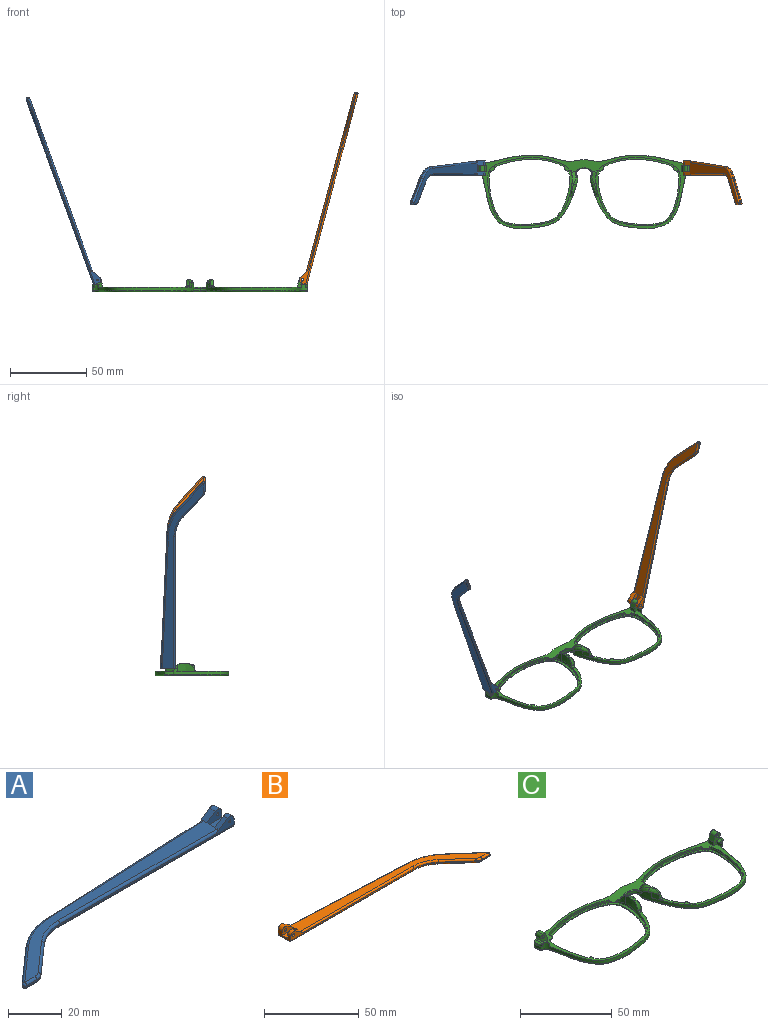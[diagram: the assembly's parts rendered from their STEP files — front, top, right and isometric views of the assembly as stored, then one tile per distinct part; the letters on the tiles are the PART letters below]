
ASSEMBLY  parts=3 mates=2
PART A: 43 faces, bbox 130.2x29.5x5.9 mm
  f0: plane 9.62x3.72mm, normal (1,0,0), area 24.7mm2, adj f1,f3,f4,f5,f10,f16,f18,f28
  f1: cylinder r=2.2mm len=3.45mm, axis (0,-1,0), area 11mm2, adj f0,f2,f4,f37
  f2: plane 6.01x3.91mm, normal (-0.55,0,0.84), area 12.7mm2, adj f1,f4,f9,f19,f37
  f3: plane 2.26x0.1mm, normal (0,0,1), area 0.1mm2, adj f0,f5,f18
  f4: plane 92.1x4.9mm, normal (0,-1,0), area 79.9mm2, adj f0,f1,f2,f14,f19,f36,f42
  f5: plane 93.42x4.13mm, normal (-0.04,1,0), area 64.8mm2, adj f0,f3,f11,f15,f17,f27,f28
  f6: plane 17.82x15.72mm, normal (-0.66,0.75,0), area 14.3mm2, adj f11,f12,f25,f30
  f7: plane 5.46x0.6mm, normal (0,-1,0), area 3.3mm2, adj f12,f13,f23,f32
  f8: plane 14.99x13.23mm, normal (0.66,-0.75,0), area 12mm2, adj f13,f14,f21,f34
  f9: plane 121.18x26.73mm, normal (0,0,1), area 627.7mm2, adj f2,f17,f19,f20,f21,f22,f23,f25
  f10: plane 129.1x27.08mm, normal (0,0,-1), area 686.5mm2, adj f0,f28,f29,f30,f32,f33,f34,f35
  f11: cylinder r=30mm len=18.52mm, axis (0,0,-1), area 12.2mm2, adj f5,f6,f26,f29
  f12: cylinder r=1mm len=1.75mm, axis (0,0,-1), area 1.5mm2, adj f6,f7,f24,f31
  f13: cylinder r=5mm len=3.31mm, axis (0,0,-1), area 2.2mm2, adj f7,f8,f22,f33
  f14: cylinder r=20mm len=13.23mm, axis (0,0,1), area 8.7mm2, adj f4,f8,f20,f35
  f15: plane 5.66x0.25mm, normal (0,0,-1), area 0.7mm2, adj f5,f17,f18
  f16: cylinder r=2.2mm len=3.45mm, axis (0,-1,0), area 14.8mm2, adj f0,f17,f18,f38
  f17: plane 6.01x3.91mm, normal (-0.55,0,0.84), area 16.9mm2, adj f5,f9,f15,f16,f18,f27,f38
  f18: plane 7.92x3.3mm, normal (0,1,0), area 15.9mm2, adj f0,f3,f15,f16,f17,f41
  f19: cylinder r=1mm len=84.18mm, axis (-1,0,0), area 131.4mm2, adj f2,f4,f9,f20
  f20: torus R=21mm, axis (0,0,1), area 23.1mm2, adj f9,f14,f19,f21
  f21: cylinder r=1mm len=15.65mm, axis (-0.75,-0.66,0), area 31.4mm2, adj f8,f9,f20,f22
  f22: torus R=4mm, axis (0,0,1), area 5.3mm2, adj f9,f13,f21,f23
  f23: cylinder r=1mm len=5.46mm, axis (-1,0,0), area 8.6mm2, adj f7,f9,f22,f24
  f24: sphere r=1mm, area 2.4mm2, adj f12,f23,f25
  f25: cylinder r=1mm len=18.48mm, axis (0.75,0.66,0), area 37.3mm2, adj f6,f9,f24,f26
  f26: torus R=29mm, axis (0,0,1), area 31.6mm2, adj f9,f11,f25,f27
  f27: cylinder r=1mm len=85.5mm, axis (1,0.04,0), area 133.5mm2, adj f5,f9,f17,f26
  f28: cylinder r=1mm len=93.46mm, axis (-1,-0.04,0), area 146.9mm2, adj f0,f5,f10,f29
  f29: torus R=29mm, axis (0,0,1), area 31.6mm2, adj f10,f11,f28,f30
  f30: cylinder r=1mm len=18.48mm, axis (-0.75,-0.66,0), area 37.3mm2, adj f6,f10,f29,f31
  f31: sphere r=1mm, area 2.4mm2, adj f12,f30,f32
  f32: cylinder r=1mm len=5.46mm, axis (1,0,0), area 8.6mm2, adj f7,f10,f31,f33
  f33: torus R=4mm, axis (0,0,1), area 5.3mm2, adj f10,f13,f32,f34
  f34: cylinder r=1mm len=15.65mm, axis (0.75,0.66,0), area 31.4mm2, adj f8,f10,f33,f35
  f35: torus R=21mm, axis (0,0,1), area 23.1mm2, adj f10,f14,f34,f36
  f36: cylinder r=1mm len=92.1mm, axis (1,0,0), area 144.7mm2, adj f0,f4,f10,f35
  f37: plane 7.92x4.7mm, normal (0,1,0), area 27mm2, adj f0,f1,f2,f39,f40,f42
  f38: plane 7.92x4.7mm, normal (0,-1,0), area 27mm2, adj f0,f16,f17,f39,f40,f41
  f39: plane 7.92x4.1mm, normal (0,0,1), area 32.5mm2, adj f0,f37,f38,f40
  f40: plane 4.1x1.4mm, normal (1,0,0), area 5.7mm2, adj f9,f37,f38,f39
  f41: cylinder r=0.5mm len=3.1mm, axis (0,-1,0), area 9.7mm2, adj f18,f38
  f42: cylinder r=0.5mm len=2.3mm, axis (0,-1,0), area 7.2mm2, adj f4,f37
PART B: 43 faces, bbox 130.2x29.5x5.9 mm
  f0: plane 9.62x3.72mm, normal (-1,0,0), area 24.7mm2, adj f1,f3,f4,f5,f10,f16,f18,f28
  f1: cylinder r=2.2mm len=3.45mm, axis (0,-1,0), area 11mm2, adj f0,f2,f4,f37
  f2: plane 6.01x3.91mm, normal (0.55,0,0.84), area 12.7mm2, adj f1,f4,f9,f19,f37
  f3: plane 2.26x0.1mm, normal (0,0,1), area 0.1mm2, adj f0,f5,f18
  f4: plane 92.1x4.9mm, normal (0,-1,0), area 78.2mm2, adj f0,f1,f2,f14,f19,f36,f42
  f5: plane 93.42x4.13mm, normal (0.04,1,0), area 64.8mm2, adj f0,f3,f11,f15,f17,f27,f28
  f6: plane 17.82x15.72mm, normal (0.66,0.75,0), area 14.3mm2, adj f11,f12,f25,f30
  f7: plane 5.46x0.6mm, normal (0,-1,0), area 3.3mm2, adj f12,f13,f23,f32
  f8: plane 14.99x13.23mm, normal (-0.66,-0.75,0), area 12mm2, adj f13,f14,f21,f34
  f9: plane 121.18x26.73mm, normal (0,0,1), area 627.7mm2, adj f2,f17,f19,f20,f21,f22,f23,f25
  f10: plane 129.1x27.08mm, normal (0,0,-1), area 686.5mm2, adj f0,f28,f29,f30,f32,f33,f34,f35
  f11: cylinder r=30mm len=18.52mm, axis (0,0,-1), area 12.2mm2, adj f5,f6,f26,f29
  f12: cylinder r=1mm len=1.75mm, axis (0,0,-1), area 1.5mm2, adj f6,f7,f24,f31
  f13: cylinder r=5mm len=3.31mm, axis (0,0,-1), area 2.2mm2, adj f7,f8,f22,f33
  f14: cylinder r=20mm len=13.23mm, axis (0,0,1), area 8.7mm2, adj f4,f8,f20,f35
  f15: plane 5.66x0.25mm, normal (0,0,-1), area 0.7mm2, adj f5,f17,f18
  f16: cylinder r=2.2mm len=3.45mm, axis (0,-1,0), area 14.8mm2, adj f0,f17,f18,f38
  f17: plane 6.01x3.91mm, normal (0.55,0,0.84), area 16.9mm2, adj f5,f9,f15,f16,f18,f27,f38
  f18: plane 7.92x3.3mm, normal (0,1,0), area 14.3mm2, adj f0,f3,f15,f16,f17,f41
  f19: cylinder r=1mm len=84.18mm, axis (1,0,0), area 131.4mm2, adj f2,f4,f9,f20
  f20: torus R=21mm, axis (0,0,1), area 23.1mm2, adj f9,f14,f19,f21
  f21: cylinder r=1mm len=15.65mm, axis (0.75,-0.66,0), area 31.4mm2, adj f8,f9,f20,f22
  f22: torus R=4mm, axis (0,0,1), area 5.3mm2, adj f9,f13,f21,f23
  f23: cylinder r=1mm len=5.46mm, axis (1,0,0), area 8.6mm2, adj f7,f9,f22,f24
  f24: sphere r=1mm, area 2.4mm2, adj f12,f23,f25
  f25: cylinder r=1mm len=18.48mm, axis (-0.75,0.66,0), area 37.3mm2, adj f6,f9,f24,f26
  f26: torus R=29mm, axis (0,0,1), area 31.6mm2, adj f9,f11,f25,f27
  f27: cylinder r=1mm len=85.5mm, axis (-1,0.04,0), area 133.5mm2, adj f5,f9,f17,f26
  f28: cylinder r=1mm len=93.46mm, axis (1,-0.04,0), area 146.9mm2, adj f0,f5,f10,f29
  f29: torus R=29mm, axis (0,0,1), area 31.6mm2, adj f10,f11,f28,f30
  f30: cylinder r=1mm len=18.48mm, axis (0.75,-0.66,0), area 37.3mm2, adj f6,f10,f29,f31
  f31: sphere r=1mm, area 2.4mm2, adj f12,f30,f32
  f32: cylinder r=1mm len=5.46mm, axis (-1,0,0), area 8.6mm2, adj f7,f10,f31,f33
  f33: torus R=4mm, axis (0,0,1), area 5.3mm2, adj f10,f13,f32,f34
  f34: cylinder r=1mm len=15.65mm, axis (-0.75,0.66,0), area 31.4mm2, adj f8,f10,f33,f35
  f35: torus R=21mm, axis (0,0,1), area 23.1mm2, adj f10,f14,f34,f36
  f36: cylinder r=1mm len=92.1mm, axis (-1,0,0), area 144.7mm2, adj f0,f4,f10,f35
  f37: plane 7.92x4.7mm, normal (0,1,0), area 25.4mm2, adj f0,f1,f2,f39,f40,f42
  f38: plane 7.92x4.7mm, normal (0,-1,0), area 25.4mm2, adj f0,f16,f17,f39,f40,f41
  f39: plane 7.92x4.1mm, normal (0,0,1), area 32.5mm2, adj f0,f37,f38,f40
  f40: plane 4.1x1.4mm, normal (-1,0,0), area 5.7mm2, adj f9,f37,f38,f39
  f41: cylinder r=0.88mm len=3.1mm, axis (0,-1,0), area 17mm2, adj f18,f38
  f42: cylinder r=0.88mm len=2.3mm, axis (0,-1,0), area 12.6mm2, adj f4,f37
PART C: 115 faces, bbox 141.9x48.6x10.2 mm
  f0: plane 2.1x0.75mm, normal (-0.99,-0.13,0), area 0.8mm2, adj f1,f112,f113,f114
  f1: cone r=1mm half-angle=20deg, axis (0,0,1), area 3.8mm2, adj f0,f2,f111,f114
  f2: plane 141.2x48.5mm, normal (0,0,1), area 725.6mm2, adj f1,f3,f4,f5,f6,f14,f15,f16
  f3: cylinder r=1mm len=2.28mm, axis (-0.34,0,-0.94), area 3mm2, adj f2,f4,f111,f114
  f4: plane 3.41x2.1mm, normal (0,1,0), area 6.4mm2, adj f2,f3,f5,f113,f114
  f5: plane 2.1x0.14mm, normal (-1,0,0), area 0.3mm2, adj f2,f4,f6,f113
  f6: plane 6.96x5.07mm, normal (0,1,0), area 20.8mm2, adj f2,f5,f7,f8,f10,f11,f12,f13
  f7: plane 4x0.04mm, normal (0.34,0,0.94), area 0.2mm2, adj f6,f12,f14,f15
  f8: plane 4x2.21mm, normal (0.94,0,-0.34), area 9.4mm2, adj f6,f9,f10,f113
  f9: plane 5.45x5.04mm, normal (0,-1,0), area 16.2mm2, adj f8,f10,f11,f12,f13,f15,f16,f113
  f10: cylinder r=1.98mm len=4mm, axis (0,-1,0), area 12.4mm2, adj f6,f8,f9,f11
  f11: cylinder r=1.98mm len=4mm, axis (0,1,0), area 12.4mm2, adj f6,f9,f10,f12
  f12: plane 4x3.31mm, normal (-0.94,0,0.34), area 14.1mm2, adj f6,f7,f9,f11
  f13: cylinder r=0.88mm len=4mm, axis (0,-1,0), area 22mm2, adj f6,f9
  f14: plane 4x2.36mm, normal (-1,0,0), area 9.5mm2, adj f2,f6,f7,f15
  f15: plane 2.36x2.35mm, normal (0,-1,0), area 4.5mm2, adj f2,f7,f9,f14,f16
  f16: plane 4.04x2.1mm, normal (-1,0,0), area 8.5mm2, adj f2,f9,f15,f112,f113
  f17: cylinder r=1mm len=1mm, axis (1,0,0), area 0.6mm2, adj f2,f18,f31,f112
  f18: plane 1x0.55mm, normal (0,-1,0), area 0.3mm2, adj f17,f19,f29
  f19: bspline ~6.85x6.85mm, area 10.8mm2, adj f18,f20,f28,f29,f31,f38
  f20: bspline ~9.24x4.72mm, area 14.8mm2, adj f19,f21,f28,f29,f112
  f21: bspline ~9.31x5.64mm, area 17.9mm2, adj f20,f22,f24,f26,f112
  f22: extruded ~1.18x1.14mm, area 1.3mm2, adj f21,f23,f24,f112
  f23: plane 1.23x0.28mm, normal (0,0,1), area 0mm2, adj f22,f112
  f24: bspline ~2.83x2.53mm, area 1mm2, adj f21,f22,f25,f61,f112
  f25: bspline ~1.64x1.15mm, area 0.6mm2, adj f24,f61,f62,f112
  f26: bspline ~12.06x7.53mm, area 21.7mm2, adj f21,f27,f28,f38,f61
  f27: extruded ~4.46x0.33mm, area 1.5mm2, adj f26,f38
  f28: plane 3.84x1.19mm, normal (0,0,1), area 2.2mm2, adj f19,f20,f26,f38
  f29: extruded ~4.55x3.15mm, area 14.7mm2, adj f18,f19,f20,f30,f112
  f30: plane 4.6x1.59mm, normal (0,0,1), area 0.2mm2, adj f29,f112
  f31: bspline ~2.52x1.35mm, area 2.4mm2, adj f2,f17,f19,f38
  f32: cylinder r=1.3mm len=2.35mm, axis (0,0,1), area 2mm2, adj f2,f33,f38
  f33: plane 2.36x2.1mm, normal (0,0,-1), area 2.8mm2, adj f32,f38
  f34: cylinder r=1.3mm len=2.42mm, axis (0,0,1), area 2mm2, adj f2,f35,f38
  f35: plane 2.44x1.87mm, normal (0,0,-1), area 2.6mm2, adj f34,f38
  f36: cylinder r=2.28mm len=3.71mm, axis (0,0,1), area 3.2mm2, adj f2,f37,f38
  f37: plane 3.73x3.57mm, normal (0,0,-1), area 7.5mm2, adj f36,f38
  f38: extruded ~55.28x44.82mm, area 217.8mm2, adj f2,f19,f26,f27,f28,f31,f32,f33
  f39: extruded ~55.28x44.82mm, area 160.5mm2, adj f38,f40
  f40: plane 56.1x45.06mm, normal (0,0,1), area 185.4mm2, adj f39,f41
  f41: bspline ~54.86x44.62mm, area 251.2mm2, adj f40,f42
  f42: plane 138.71x46.15mm, normal (0,0,-1), area 518.1mm2, adj f41,f43,f46,f50,f51,f52,f53,f55
  f43: bspline ~54.86x44.62mm, area 251.2mm2, adj f42,f44
  f44: plane 56.1x45.06mm, normal (0,0,1), area 185.4mm2, adj f43,f45
  f45: extruded ~55.28x44.82mm, area 160.5mm2, adj f44,f86
  f46: bspline ~5.09x1.3mm, area 7mm2, adj f42,f47,f48,f49,f112
  f47: bspline ~1x0.99mm, area 0.7mm2, adj f46,f58,f112
  f48: bspline ~0.6x0.43mm, area 0mm2, adj f46,f50
  f49: bspline ~0.99x0.94mm, area 0.5mm2, adj f46,f50,f112
  f50: bspline ~34.89x7.19mm, area 52.8mm2, adj f42,f48,f49,f51,f112
  f51: bspline ~37.4x5.09mm, area 57.7mm2, adj f42,f50,f52,f110
  f52: bspline ~37.4x5.09mm, area 57.7mm2, adj f42,f51,f53,f109
  f53: bspline ~34.89x7.19mm, area 52.8mm2, adj f42,f52,f54,f108
  f54: bspline ~1x0.99mm, area 0.6mm2, adj f53,f55,f108
  f55: bspline ~4.91x1.27mm, area 7mm2, adj f42,f54,f56,f108
  f56: bspline ~1x0.99mm, area 0.7mm2, adj f55,f57,f108
  f57: bspline ~70.13x40.43mm, area 184.3mm2, adj f42,f56,f58,f108
  f58: bspline ~70.13x40.43mm, area 184.3mm2, adj f42,f47,f57,f112
  f59: plane 3.81x3.79mm, normal (0,0,-1), area 8.1mm2, adj f38,f60
  f60: cylinder r=2.28mm len=3.79mm, axis (0,0,1), area 3.4mm2, adj f2,f38,f59
  f61: bspline ~5.43x2.98mm, area 4.2mm2, adj f2,f24,f25,f26,f38
  f62: bspline ~6.43x3.32mm, area 5mm2, adj f2,f25,f63,f112
  f63: bspline ~6.43x3.32mm, area 5mm2, adj f2,f62,f64,f108
  f64: bspline ~1.64x1.15mm, area 0.6mm2, adj f63,f65,f77,f108
  f65: bspline ~2.83x2.53mm, area 1mm2, adj f64,f66,f75,f77,f108
  f66: bspline ~9.31x5.63mm, area 17.9mm2, adj f65,f67,f73,f75,f108
  f67: bspline ~9.24x4.72mm, area 14.8mm2, adj f66,f68,f69,f72,f108
  f68: plane 3.84x1.19mm, normal (0,0,1), area 2.2mm2, adj f67,f72,f73,f86
  f69: extruded ~4.55x3.15mm, area 14.7mm2, adj f67,f70,f71,f72,f108
  f70: plane 4.6x1.59mm, normal (0,0,1), area 0.2mm2, adj f69,f108
  f71: plane 1x0.55mm, normal (0,-1,0), area 0.3mm2, adj f69,f72,f88
  f72: bspline ~6.85x6.85mm, area 10.9mm2, adj f67,f68,f69,f71,f86,f87
  f73: bspline ~12.06x7.53mm, area 21.7mm2, adj f66,f68,f74,f77,f86
  f74: extruded ~4.46x0.33mm, area 1.5mm2, adj f73,f86
  f75: extruded ~1.18x1.14mm, area 1.3mm2, adj f65,f66,f76,f108
  f76: plane 1.23x0.28mm, normal (0,0,1), area 0mm2, adj f75,f108
  f77: bspline ~5.43x2.98mm, area 4.2mm2, adj f2,f64,f65,f73,f86
  f78: cylinder r=2.28mm len=3.79mm, axis (0,0,1), area 3.4mm2, adj f2,f79,f86
  f79: plane 3.81x3.79mm, normal (0,0,-1), area 8.1mm2, adj f78,f86
  f80: cylinder r=2.28mm len=3.71mm, axis (0,0,1), area 3.2mm2, adj f2,f81,f86
  f81: plane 3.73x3.57mm, normal (0,0,-1), area 7.5mm2, adj f80,f86
  f82: cylinder r=1.3mm len=2.42mm, axis (0,0,1), area 2mm2, adj f2,f83,f86
  f83: plane 2.44x1.87mm, normal (0,0,-1), area 2.6mm2, adj f82,f86
  f84: cylinder r=1.3mm len=2.35mm, axis (0,0,1), area 2mm2, adj f2,f85,f86
  f85: plane 2.36x2.1mm, normal (0,0,-1), area 2.8mm2, adj f84,f86
  f86: extruded ~55.28x44.82mm, area 217.3mm2, adj f2,f45,f68,f72,f73,f74,f77,f78
  f87: bspline ~2.52x1.35mm, area 2.4mm2, adj f2,f72,f86,f88
  f88: cylinder r=1mm len=1mm, axis (-1,0,0), area 0.6mm2, adj f2,f71,f87,f108
  f89: plane 4.04x2.1mm, normal (1,0,0), area 8.5mm2, adj f2,f90,f98,f100,f108
  f90: plane 8.23x3.03mm, normal (0,0,1), area 11.3mm2, adj f89,f91,f92,f97,f98,f102,f103,f104
  f91: plane 6.33x1.62mm, normal (-0.34,0,0.94), area 8.1mm2, adj f90,f97,f104,f105,f106,f107
  f92: plane 4x2.21mm, normal (-0.94,0,-0.34), area 9.4mm2, adj f90,f93,f98,f102
  f93: cylinder r=1.98mm len=4mm, axis (0,-1,0), area 12.4mm2, adj f92,f94,f98,f102
  f94: cylinder r=1.98mm len=4mm, axis (0,1,0), area 12.4mm2, adj f93,f95,f98,f102
  f95: plane 4x3.31mm, normal (0.94,0,0.34), area 14.1mm2, adj f94,f96,f98,f102
  f96: plane 4x0.04mm, normal (-0.34,0,0.94), area 0.2mm2, adj f95,f100,f101,f102
  f97: plane 2.1x0.75mm, normal (0.99,-0.13,0), area 0.8mm2, adj f90,f91,f107,f108
  f98: plane 5.45x5.04mm, normal (0,-1,0), area 16.2mm2, adj f89,f90,f92,f93,f94,f95,f99,f100
  f99: cylinder r=0.88mm len=4mm, axis (0,-1,0), area 22mm2, adj f98,f102
  f100: plane 2.36x2.35mm, normal (0,-1,0), area 4.5mm2, adj f2,f89,f96,f98,f101
  f101: plane 4x2.36mm, normal (1,0,0), area 9.5mm2, adj f2,f96,f100,f102
  f102: plane 6.96x5.07mm, normal (0,1,0), area 20.8mm2, adj f2,f90,f92,f93,f94,f95,f96,f99
  f103: plane 2.1x0.14mm, normal (1,0,0), area 0.3mm2, adj f2,f90,f102,f104
  f104: plane 3.41x2.1mm, normal (0,1,0), area 6.4mm2, adj f2,f90,f91,f103,f105
  f105: cylinder r=1mm len=2.28mm, axis (0.34,0,-0.94), area 3mm2, adj f2,f91,f104,f106
  f106: plane 3.34x1.6mm, normal (-0.94,0,-0.34), area 5.7mm2, adj f2,f91,f105,f107
  f107: cone r=1mm half-angle=20deg, axis (0,0,1), area 3.8mm2, adj f2,f91,f97,f106
  f108: extruded ~70.11x48.13mm, area 338mm2, adj f2,f53,f54,f55,f56,f57,f63,f64
  f109: extruded ~36.27x4.08mm, area 73.6mm2, adj f2,f52,f108,f110
  f110: extruded ~36.27x4.08mm, area 73.6mm2, adj f2,f51,f109,f112
  f111: plane 3.34x1.6mm, normal (0.94,0,-0.34), area 5.7mm2, adj f1,f2,f3,f114
  f112: extruded ~70.11x48.13mm, area 337.9mm2, adj f0,f2,f16,f17,f20,f21,f22,f23
  f113: plane 8.23x3.03mm, normal (0,0,1), area 11.3mm2, adj f0,f4,f5,f6,f8,f9,f16,f112
  f114: plane 6.33x1.62mm, normal (0.34,0,0.94), area 8.1mm2, adj f0,f1,f3,f4,f111,f113
PLACE A rot(axis=(0,1,0),70deg) t=(-76.79,-5.75,56)mm
PLACE B rot(axis=(0,-1,0),75deg) t=(68.2,-5.75,-61.61)mm
PLACE C t=(14.15,-3.13,-5.77)mm
MATE revolute A.f1 <-> C.f94  axis (0,-1,0) through (-52.91,2.72,1.21)mm
MATE revolute B.f41 <-> C.f10  axis (0,-1,0) through (81.2,2.72,1.21)mm
